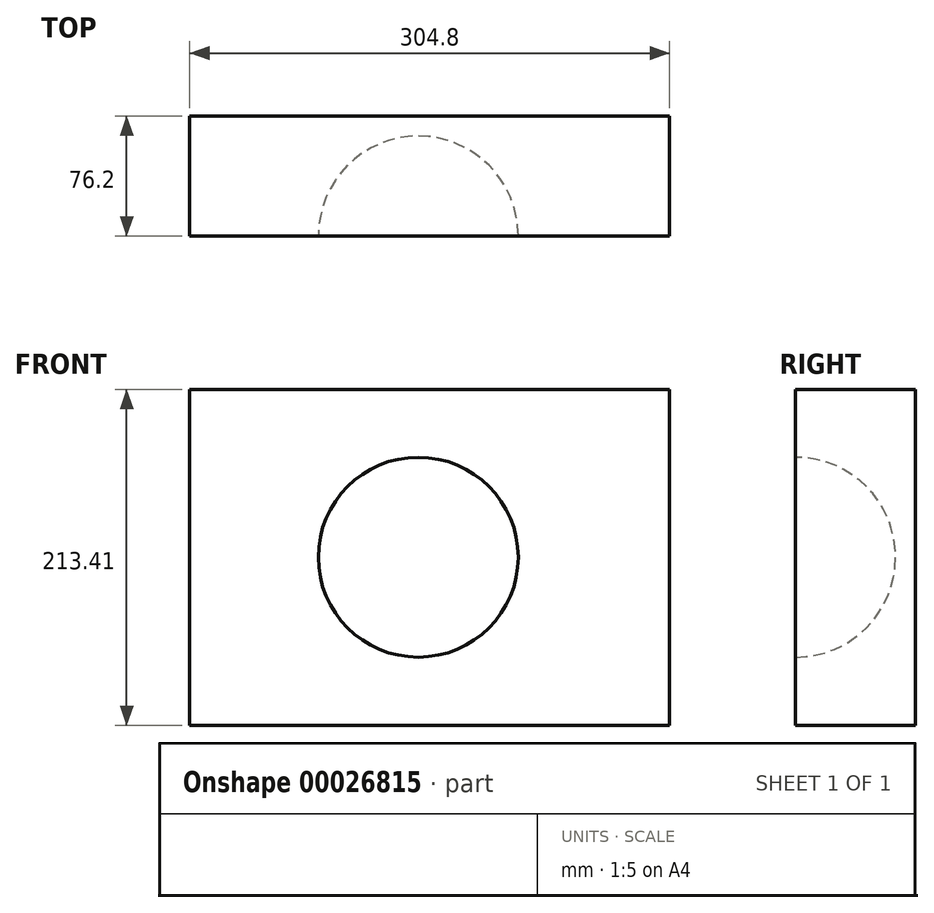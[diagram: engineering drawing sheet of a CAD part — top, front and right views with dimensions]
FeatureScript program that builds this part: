
annotation { "Feature Type Name" : "Feature", "Feature Type Description" : "" }
export const myFeature = defineFeature(function(context is Context, id is Id, definition is map)
    precondition{}
    {
        {
            var Q0;
            Q0=qCreatedBy(makeId("Front.planeOp"),FACE);
            var sketch = newSketch(context, id + "F0", { "sketchPlane" : qUnion([Q0])});
            skLineSegment(sketch, "E0.bottom", {"start": v(-151.96, 107.48) * mm, "end": v(152.84, 107.48) * mm});
            skLineSegment(sketch, "E0.top", {"start": v(-151.96, -105.93) * mm, "end": v(152.84, -105.93) * mm});
            skLineSegment(sketch, "E0.left", {"start": v(-151.96, 107.48) * mm, "end": v(-151.96, -105.93) * mm});
            skLineSegment(sketch, "E0.right", {"start": v(152.84, 107.48) * mm, "end": v(152.84, -105.93) * mm});
            skSolve(sketch);
        }
        {
            var Q0;
            Q0=makeQuery(id+"F0.imprint","IMPRINT",FACE,{"disambiguationData":[TD([[makeQuery(id+"F0.imprint","IMPRINT",EDGE,{"derivedFrom":sQuery(id+"F0.wireOp",EDGE,"E0.bottom")}),-1.0]])]});
            extrude(context, id + "F1", {"entities" : qUnion([Q0]), "depth" : 76.2 * mm});
        }
        {
            var Q0;
            Q0=makeQuery(id+"F1.opExtrude","CAP_FACE",FACE,{"disambiguationData":[OSD([sQuery(id+"F0.wireOp",EDGE,"E0.bottom"),sQuery(id+"F0.wireOp",EDGE,"E0.top"),sQuery(id+"F0.wireOp",EDGE,"E0.left"),sQuery(id+"F0.wireOp",EDGE,"E0.right")])],"isStart":false});
            var sketch = newSketch(context, id + "F2", { "sketchPlane" : qUnion([Q0])});
            skArc(sketch, "E1", {"start": v(-6.86, -62.55) * mm, "mid": v(56.64, 0.95) * mm, "end": v(-6.86, 64.45) * mm});
            skLineSegment(sketch, "E2", {"start": v(-6.86, 64.45) * mm, "end": v(-6.86, -62.55) * mm});
            skSolve(sketch);
        }
        {
            var Q0;
            Q0 = qSketchRegion(id + "F2", true);
            var Q1;
            Q1=sQuery(id+"F2.wireOp",EDGE,"E2");
            revolve(context, id + "F3", {"operationType" : NewBodyOperationType.REMOVE, "entities" : qUnion([Q0]), "axis" : qUnion([Q1]), "revolveType" : RevolveType.FULL, "oppositeDirection" : true});
        }
    });
